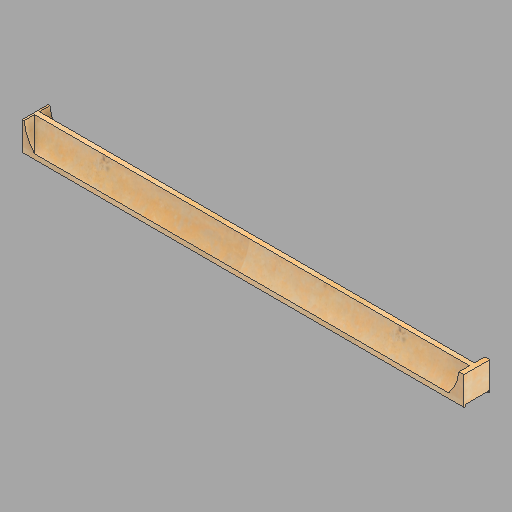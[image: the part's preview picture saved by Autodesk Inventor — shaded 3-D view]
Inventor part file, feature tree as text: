
AUTODESK INVENTOR PART (.ipt)
format: ipt  version: 2022.2 (Build 262287010, 287A)  size: 180,224 bytes
history: native  units: in
note: dims shown in document units (in); Inventor stores cm internally (conversion verified against a paired STEP export)
features: direct_edit x1, other x1, revolve x1
ambient origin geometry x8: Origin, YZ Plane, XZ Plane, XY Plane, X Axis, Y Axis, Z Axis, Center Point
bodies: Solid1 (feature_tree)
feature tree (3):
  direct_edit  "Direct Edit1"
  other  "Transom (R) (1)"
  revolve  "Rotate1"  [1 undecoded]
note: 1 required parameter value undecoded (feature->parameter linkage not recoverable at this tier; creation-order binding heuristic only, values carry confidence <= 0.55)
